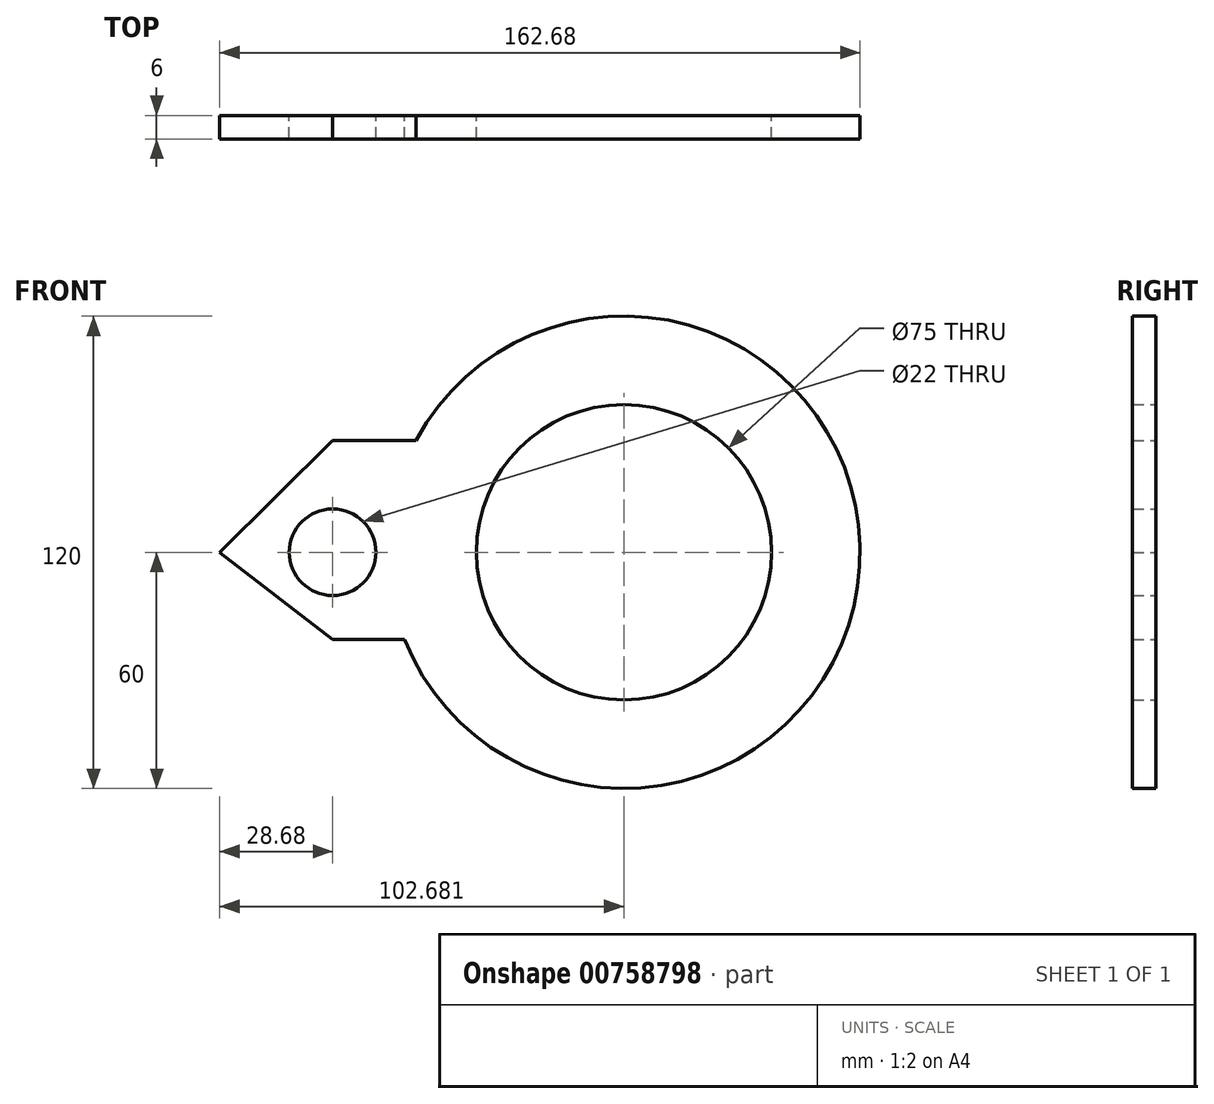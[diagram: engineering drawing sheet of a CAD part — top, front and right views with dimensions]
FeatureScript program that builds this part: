
annotation { "Feature Type Name" : "Feature", "Feature Type Description" : "" }
export const myFeature = defineFeature(function(context is Context, id is Id, definition is map)
    precondition{}
    {
        {
            var Q0;
            Q0=qCreatedBy(makeId("Front.planeOp"),FACE);
            var sketch = newSketch(context, id + "F0", { "sketchPlane" : qUnion([Q0])});
            skCircle(sketch, "E0", {"center": v(0, 0) * mm, "radius": 11 * mm});
            skCircle(sketch, "E1", {"center": v(74, 0) * mm, "radius": 60 * mm});
            skCircle(sketch, "E2", {"center": v(74, 0) * mm, "radius": 37.5 * mm});
            skLineSegment(sketch, "E3", {"start": v(21.18, 28.46) * mm, "end": v(0, 28.46) * mm});
            skLineSegment(sketch, "E4", {"start": v(0, 28.46) * mm, "end": v(-28.68, 0) * mm});
            skLineSegment(sketch, "E5", {"start": v(-28.68, 0) * mm, "end": v(0, -22.14) * mm});
            skLineSegment(sketch, "E6", {"start": v(0, -22.14) * mm, "end": v(18.23, -22.14) * mm});
            skSolve(sketch);
        }
        {
            var Q0;
            Q0=makeQuery(id+"F0.imprint","IMPRINT",FACE,{"disambiguationData":[TD([[makeQuery(id+"F0.imprint","IMPRINT",EDGE,{"derivedFrom":sQuery(id+"F0.wireOp",EDGE,"E2")}),-1.0]])]});
            var Q1;
            Q1=makeQuery(id+"F0.imprint","IMPRINT",FACE,{"disambiguationData":[TD([[makeQuery(id+"F0.imprint","IMPRINT",EDGE,{"derivedFrom":sQuery(id+"F0.wireOp",EDGE,"ZBid1YPj-d3Dq-uqsu-D7ZK-bMhDYMGsZLm6")}),1.0]])]});
            var Q2;
            Q2=makeQuery(id+"F0.imprint","IMPRINT",FACE,{"disambiguationData":[TD([[makeQuery(id+"F0.imprint","IMPRINT",EDGE,{"derivedFrom":sQuery(id+"F0.wireOp",EDGE,"E0")}),-1.0]])]});
            var Q3;
            Q3=makeQuery(id+"F0.imprint","IMPRINT",FACE,{"disambiguationData":[TD([[makeQuery(id+"F0.imprint","IMPRINT",EDGE,{"derivedFrom":sQuery(id+"F0.wireOp",EDGE,"yz0U1OBn-RngI-s16I-3zWG-rRK4JuJQmH3T")}),-1.0]])]});
            extrude(context, id + "F1", {"entities" : qUnion([Q0, Q1, Q2, Q3]), "depth" : 6 * mm, "offsetDistance" : 25 * mm});
        }
    });
